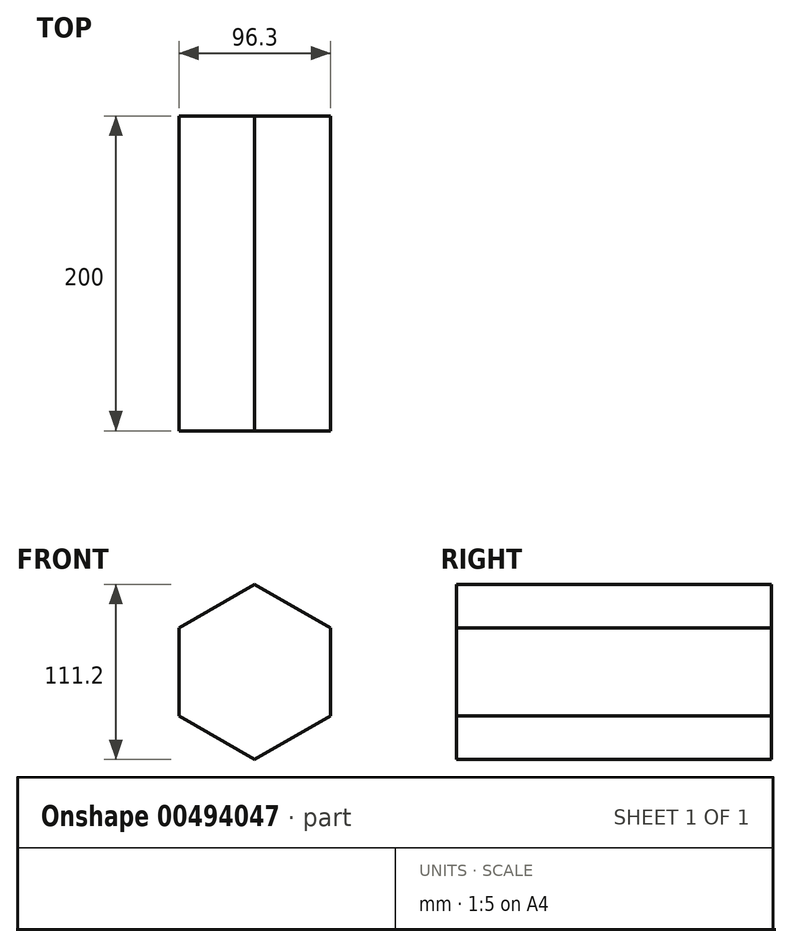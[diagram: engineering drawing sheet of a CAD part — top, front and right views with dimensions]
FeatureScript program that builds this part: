
annotation { "Feature Type Name" : "Feature", "Feature Type Description" : "" }
export const myFeature = defineFeature(function(context is Context, id is Id, definition is map)
    precondition{}
    {
        {
            var Q0;
            Q0=qCreatedBy(makeId("Front.planeOp"),FACE);
            var sketch = newSketch(context, id + "F0", { "sketchPlane" : qUnion([Q0])});
            skCircle(sketch, "E0.cCircle", {"center": v(0, 0) * mm, "radius": 55.6 * mm, "construction": true});
            skLineSegment(sketch, "E0.0", {"start": v(0, 55.6) * mm, "end": v(48.15, 27.8) * mm});
            skLineSegment(sketch, "E0.1", {"start": v(48.15, 27.8) * mm, "end": v(48.15, -27.8) * mm});
            skLineSegment(sketch, "E0.2", {"start": v(48.15, -27.8) * mm, "end": v(0, -55.6) * mm});
            skLineSegment(sketch, "E0.3", {"start": v(0, -55.6) * mm, "end": v(-48.15, -27.8) * mm});
            skLineSegment(sketch, "E0.4", {"start": v(-48.15, -27.8) * mm, "end": v(-48.15, 27.8) * mm});
            skLineSegment(sketch, "E0.5", {"start": v(-48.15, 27.8) * mm, "end": v(0, 55.6) * mm});
            skSolve(sketch);
        }
        {
            var Q0;
            Q0=makeQuery(id+"F0.imprint","IMPRINT",FACE,{"disambiguationData":[TD([[makeQuery(id+"F0.imprint","IMPRINT",EDGE,{"derivedFrom":sQuery(id+"F0.wireOp",EDGE,"E0.0")}),-1.0]])]});
            extrude(context, id + "F1", {"entities" : qUnion([Q0]), "depth" : 200 * mm});
        }
    });
